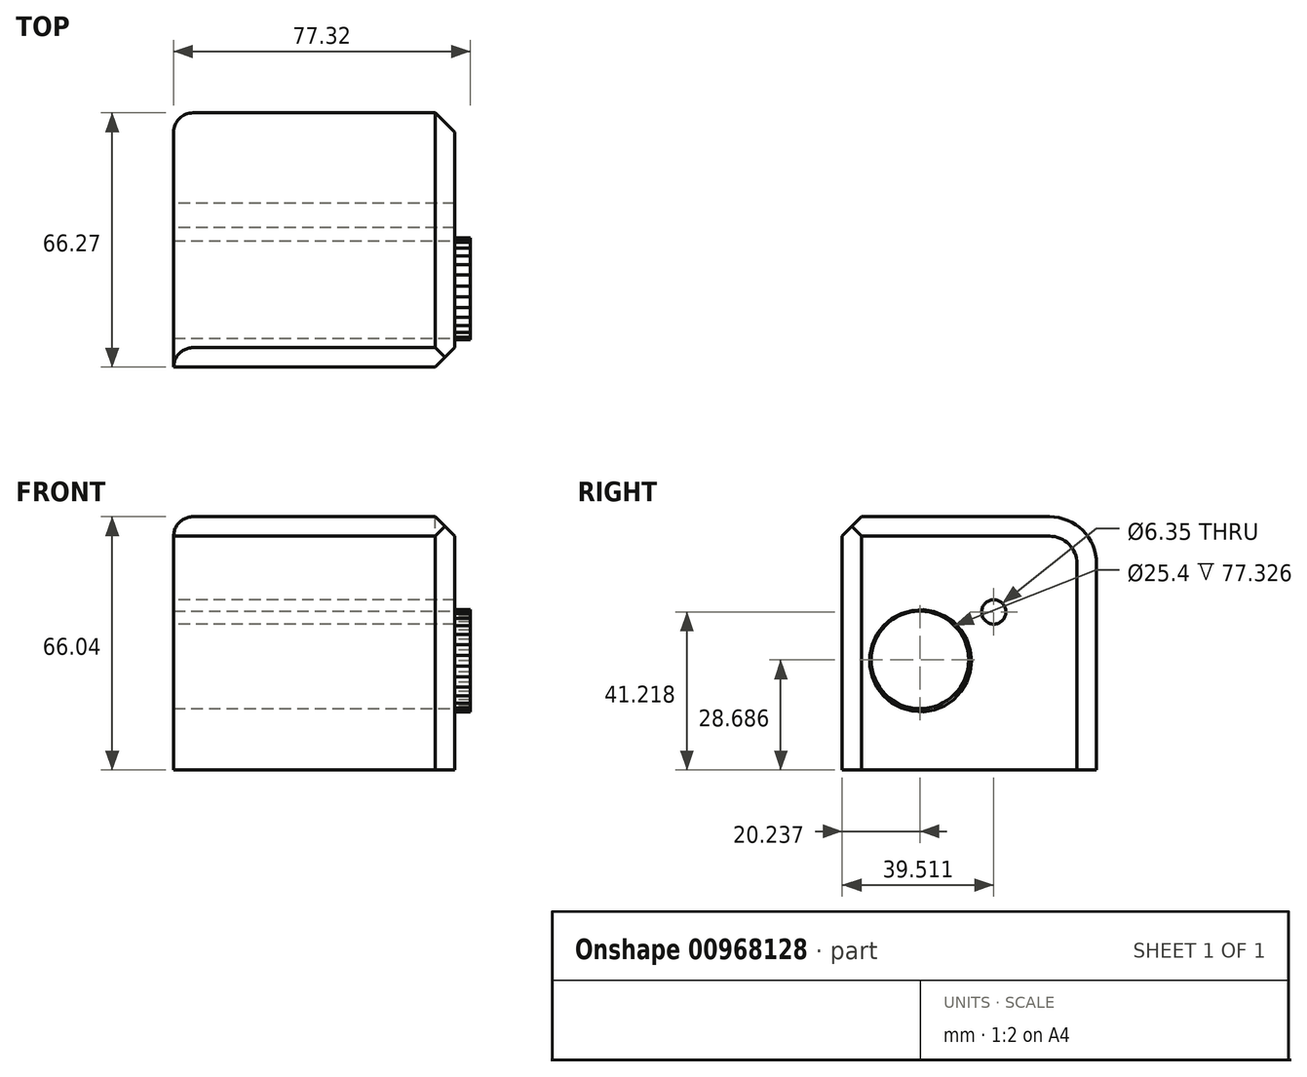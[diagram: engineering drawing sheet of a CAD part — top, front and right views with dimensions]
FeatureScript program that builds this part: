
annotation { "Feature Type Name" : "Feature", "Feature Type Description" : "" }
export const myFeature = defineFeature(function(context is Context, id is Id, definition is map)
    precondition{}
    {
        {
            var Q0;
            Q0=qCreatedBy(makeId("Top.planeOp"),FACE);
            var sketch = newSketch(context, id + "F0", { "sketchPlane" : qUnion([Q0])});
            skLineSegment(sketch, "E0", {"start": v(-34.34, 38.44) * mm, "end": v(38.92, 38.44) * mm});
            skLineSegment(sketch, "E1", {"start": v(38.92, 38.44) * mm, "end": v(38.92, -27.83) * mm});
            skLineSegment(sketch, "E2", {"start": v(38.92, -27.83) * mm, "end": v(-34.34, -27.83) * mm});
            skLineSegment(sketch, "E3", {"start": v(-34.34, -27.83) * mm, "end": v(-34.34, 38.44) * mm});
            skSolve(sketch);
        }
        {
            var Q0;
            Q0=makeQuery(id+"F0.imprint","IMPRINT",FACE,{"disambiguationData":[TD([[makeQuery(id+"F0.imprint","IMPRINT",EDGE,{"derivedFrom":sQuery(id+"F0.wireOp",EDGE,"E0")}),-1.0]])]});
            extrude(context, id + "F1", {"entities" : qUnion([Q0]), "depth" : 66.04 * mm, "offsetDistance" : 25.4 * mm});
        }
        {
            var Q0;
            Q0=makeQuery(id+"F1.opExtrude","CAP_EDGE",EDGE,{"disambiguationData":[OSD([sQuery(id+"F0.wireOp",EDGE,"E0")])],"isStart":false});
            fillet(context, id + "F2", {"entities" : qUnion([Q0]), "radius" : 12.26 * mm, "tangentPropagation" : true, "allowEdgeOverflow" : false});
        }
        {
            var Q0;
            Q0=makeQuery(id+"F1.opExtrude","SWEPT_FACE",FACE,{"disambiguationData":[OSD([sQuery(id+"F0.wireOp",EDGE,"E3")])]});
            var sketch = newSketch(context, id + "F3", { "sketchPlane" : qUnion([Q0])});
            skCircle(sketch, "E4", {"center": v(-11.68, 41.22) * mm, "radius": 9.91 * mm});
            skSolve(sketch);
        }
        {
            var Q0;
            Q0=sQuery(id+"F3.wireOp",VERTEX,"E4.center");
            var Q1;
            Q1=makeQuery(id+"F1.opExtrude","SWEPT_BODY",BODY,{"disambiguationData":[OSD([sQuery(id+"F0.wireOp",EDGE,"E0"),sQuery(id+"F0.wireOp",EDGE,"E1"),sQuery(id+"F0.wireOp",EDGE,"E2"),sQuery(id+"F0.wireOp",EDGE,"E3")])]});
            hole(context, id + "F4", {"style" : HoleStyle.SIMPLE, "endStyle" : HoleEndStyle.THROUGH, "holeDiameter" : 6.35 * mm, "majorDiameter" : 6.35 * mm, "isTappedThrough" : true, "tappedDepth" : 12.7 * mm, "tapClearance" : 3, "locations" : qUnion([Q0]), "scope" : qUnion([Q1])});
        }
        {
            var Q0;
            Q0=makeQuery(id+"F1.opExtrude","CAP_EDGE",EDGE,{"disambiguationData":[OSD([sQuery(id+"F0.wireOp",EDGE,"E2")])],"isStart":false});
            chamfer(context, id + "F5", {"entities" : qUnion([Q0]), "width" : 5.08 * mm, "tangentPropagation" : true});
        }
        {
            var Q0;
            Q0=makeQuery(id+"F1.opExtrude","SWEPT_EDGE",EDGE,{"disambiguationData":[OSD([sQuery(id+"F0.wireOp",EDGE,"E1"),sQuery(id+"F0.wireOp",EDGE,"E2")])]});
            chamfer(context, id + "F6", {"entities" : qUnion([Q0]), "width" : 5.08 * mm, "tangentPropagation" : true});
        }
        {
            var Q0;
            Q0=makeQuery(id+"F2.opFillet","BLEND_EDGE",EDGE,{"blendedFrom":[makeQuery(id+"F1.opExtrude","CAP_EDGE",EDGE,{"disambiguationData":[OSD([sQuery(id+"F0.wireOp",EDGE,"E0")])],"isStart":false}),makeQuery(id+"F1.opExtrude","SWEPT_FACE",FACE,{"disambiguationData":[OSD([sQuery(id+"F0.wireOp",EDGE,"E1")])]})],"blendedInto":[makeQuery(id+"F1.opExtrude","SWEPT_FACE",FACE,{"disambiguationData":[OSD([sQuery(id+"F0.wireOp",EDGE,"E1")])]})]});
            chamfer(context, id + "F7", {"entities" : qUnion([Q0]), "width" : 5.08 * mm, "tangentPropagation" : true});
        }
        {
            var Q0;
            Q0=makeQuery(id+"F2.opFillet","BLEND_EDGE",EDGE,{"blendedFrom":[makeQuery(id+"F1.opExtrude","CAP_EDGE",EDGE,{"disambiguationData":[OSD([sQuery(id+"F0.wireOp",EDGE,"E0")])],"isStart":false}),makeQuery(id+"F1.opExtrude","SWEPT_FACE",FACE,{"disambiguationData":[OSD([sQuery(id+"F0.wireOp",EDGE,"E3")])]})],"blendedInto":[makeQuery(id+"F1.opExtrude","SWEPT_FACE",FACE,{"disambiguationData":[OSD([sQuery(id+"F0.wireOp",EDGE,"E3")])]})]});
            fillet(context, id + "F8", {"entities" : qUnion([Q0]), "radius" : 5.08 * mm, "tangentPropagation" : true, "allowEdgeOverflow" : false});
        }
        {
            var Q0;
            Q0=makeQuery(id+"F1.opExtrude","SWEPT_FACE",FACE,{"disambiguationData":[OSD([sQuery(id+"F0.wireOp",EDGE,"E1")])]});
            var sketch = newSketch(context, id + "F9", { "sketchPlane" : qUnion([Q0])});
            skCircle(sketch, "E5.cCircle", {"center": v(-7.41, 28.47) * mm, "radius": 13.22 * mm, "construction": true});
            skLineSegment(sketch, "E5.0", {"start": v(1.2, 18.33) * mm, "end": v(-1.2, 16.72) * mm});
            skLineSegment(sketch, "E5.1", {"start": v(-1.2, 16.72) * mm, "end": v(-3.86, 15.66) * mm});
            skLineSegment(sketch, "E5.2", {"start": v(-3.86, 15.66) * mm, "end": v(-6.7, 15.2) * mm});
            skLineSegment(sketch, "E5.3", {"start": v(-6.7, 15.2) * mm, "end": v(-9.57, 15.35) * mm});
            skLineSegment(sketch, "E5.4", {"start": v(-9.57, 15.35) * mm, "end": v(-12.34, 16.12) * mm});
            skLineSegment(sketch, "E5.5", {"start": v(-12.34, 16.12) * mm, "end": v(-14.88, 17.47) * mm});
            skLineSegment(sketch, "E5.6", {"start": v(-14.88, 17.47) * mm, "end": v(-17.08, 19.33) * mm});
            skLineSegment(sketch, "E5.7", {"start": v(-17.08, 19.33) * mm, "end": v(-18.81, 21.62) * mm});
            skLineSegment(sketch, "E5.8", {"start": v(-18.81, 21.62) * mm, "end": v(-20.02, 24.23) * mm});
            skLineSegment(sketch, "E5.9", {"start": v(-20.02, 24.23) * mm, "end": v(-20.64, 27.04) * mm});
            skLineSegment(sketch, "E5.10", {"start": v(-20.64, 27.04) * mm, "end": v(-20.64, 29.92) * mm});
            skLineSegment(sketch, "E5.11", {"start": v(-20.64, 29.92) * mm, "end": v(-20.02, 32.73) * mm});
            skLineSegment(sketch, "E5.12", {"start": v(-20.02, 32.73) * mm, "end": v(-18.8, 35.34) * mm});
            skLineSegment(sketch, "E5.13", {"start": v(-18.8, 35.34) * mm, "end": v(-17.06, 37.63) * mm});
            skLineSegment(sketch, "E5.14", {"start": v(-17.06, 37.63) * mm, "end": v(-14.87, 39.49) * mm});
            skLineSegment(sketch, "E5.15", {"start": v(-14.87, 39.49) * mm, "end": v(-12.33, 40.83) * mm});
            skLineSegment(sketch, "E5.16", {"start": v(-12.33, 40.83) * mm, "end": v(-9.56, 41.6) * mm});
            skLineSegment(sketch, "E5.17", {"start": v(-9.56, 41.6) * mm, "end": v(-6.69, 41.75) * mm});
            skLineSegment(sketch, "E5.18", {"start": v(-6.69, 41.75) * mm, "end": v(-3.85, 41.29) * mm});
            skLineSegment(sketch, "E5.19", {"start": v(-3.85, 41.29) * mm, "end": v(-1.18, 40.22) * mm});
            skLineSegment(sketch, "E5.20", {"start": v(-1.18, 40.22) * mm, "end": v(1.2, 38.6) * mm});
            skLineSegment(sketch, "E5.21", {"start": v(1.2, 38.6) * mm, "end": v(3.18, 36.52) * mm});
            skLineSegment(sketch, "E5.22", {"start": v(3.18, 36.52) * mm, "end": v(4.66, 34.05) * mm});
            skLineSegment(sketch, "E5.23", {"start": v(4.66, 34.05) * mm, "end": v(5.58, 31.33) * mm});
            skLineSegment(sketch, "E5.24", {"start": v(5.58, 31.33) * mm, "end": v(5.89, 28.47) * mm});
            skLineSegment(sketch, "E5.25", {"start": v(5.89, 28.47) * mm, "end": v(5.57, 25.6) * mm});
            skLineSegment(sketch, "E5.26", {"start": v(5.57, 25.6) * mm, "end": v(4.65, 22.88) * mm});
            skLineSegment(sketch, "E5.27", {"start": v(4.65, 22.88) * mm, "end": v(3.17, 20.42) * mm});
            skLineSegment(sketch, "E5.28", {"start": v(3.17, 20.42) * mm, "end": v(1.2, 18.33) * mm});
            skPoint(sketch, "E5.0.midPoint", {"position": v(0, 17.52) * mm});
            skSolve(sketch);
        }
        {
            var Q0;
            Q0=makeQuery(id+"F9.imprint","IMPRINT",FACE,{"disambiguationData":[TD([[makeQuery(id+"F9.imprint","IMPRINT",EDGE,{"derivedFrom":sQuery(id+"F9.wireOp",EDGE,"E5.0")}),-1.0]])]});
            extrude(context, id + "F10", {"entities" : qUnion([Q0]), "operationType" : NewBodyOperationType.ADD, "depth" : 4.06 * mm, "offsetDistance" : 25.4 * mm});
        }
        {
            var Q0;
            Q0=makeQuery(id+"F10.opExtrude","CAP_FACE",FACE,{"disambiguationData":[OSD([sQuery(id+"F9.wireOp",EDGE,"E5.0"),sQuery(id+"F9.wireOp",EDGE,"E5.1"),sQuery(id+"F9.wireOp",EDGE,"E5.2"),sQuery(id+"F9.wireOp",EDGE,"E5.3"),sQuery(id+"F9.wireOp",EDGE,"E5.4"),sQuery(id+"F9.wireOp",EDGE,"E5.5"),sQuery(id+"F9.wireOp",EDGE,"E5.6"),sQuery(id+"F9.wireOp",EDGE,"E5.7"),sQuery(id+"F9.wireOp",EDGE,"E5.8"),sQuery(id+"F9.wireOp",EDGE,"E5.9"),sQuery(id+"F9.wireOp",EDGE,"E5.10"),sQuery(id+"F9.wireOp",EDGE,"E5.11"),sQuery(id+"F9.wireOp",EDGE,"E5.12"),sQuery(id+"F9.wireOp",EDGE,"E5.13"),sQuery(id+"F9.wireOp",EDGE,"E5.14"),sQuery(id+"F9.wireOp",EDGE,"E5.15"),sQuery(id+"F9.wireOp",EDGE,"E5.16"),sQuery(id+"F9.wireOp",EDGE,"E5.17"),sQuery(id+"F9.wireOp",EDGE,"E5.18"),sQuery(id+"F9.wireOp",EDGE,"E5.19"),sQuery(id+"F9.wireOp",EDGE,"E5.20"),sQuery(id+"F9.wireOp",EDGE,"E5.21"),sQuery(id+"F9.wireOp",EDGE,"E5.22"),sQuery(id+"F9.wireOp",EDGE,"E5.23"),sQuery(id+"F9.wireOp",EDGE,"E5.24"),sQuery(id+"F9.wireOp",EDGE,"E5.25"),sQuery(id+"F9.wireOp",EDGE,"E5.26"),sQuery(id+"F9.wireOp",EDGE,"E5.27"),sQuery(id+"F9.wireOp",EDGE,"E5.28")])],"isStart":false});
            var sketch = newSketch(context, id + "F11", { "sketchPlane" : qUnion([Q0])});
            skCircle(sketch, "E6", {"center": v(-7.6, 28.69) * mm, "radius": 9.42 * mm});
            skSolve(sketch);
        }
        {
            var Q0;
            Q0=sQuery(id+"F11.wireOp",VERTEX,"E6.center");
            var Q1;
            Q1=makeQuery(id+"F1.opExtrude","SWEPT_BODY",BODY,{"disambiguationData":[OSD([sQuery(id+"F0.wireOp",EDGE,"E0"),sQuery(id+"F0.wireOp",EDGE,"E1"),sQuery(id+"F0.wireOp",EDGE,"E2"),sQuery(id+"F0.wireOp",EDGE,"E3")])]});
            hole(context, id + "F12", {"style" : HoleStyle.SIMPLE, "endStyle" : HoleEndStyle.THROUGH, "holeDiameter" : 25.4 * mm, "majorDiameter" : 6.35 * mm, "isTappedThrough" : true, "tappedDepth" : 12.7 * mm, "tapClearance" : 3, "locations" : qUnion([Q0]), "scope" : qUnion([Q1])});
        }
    });
